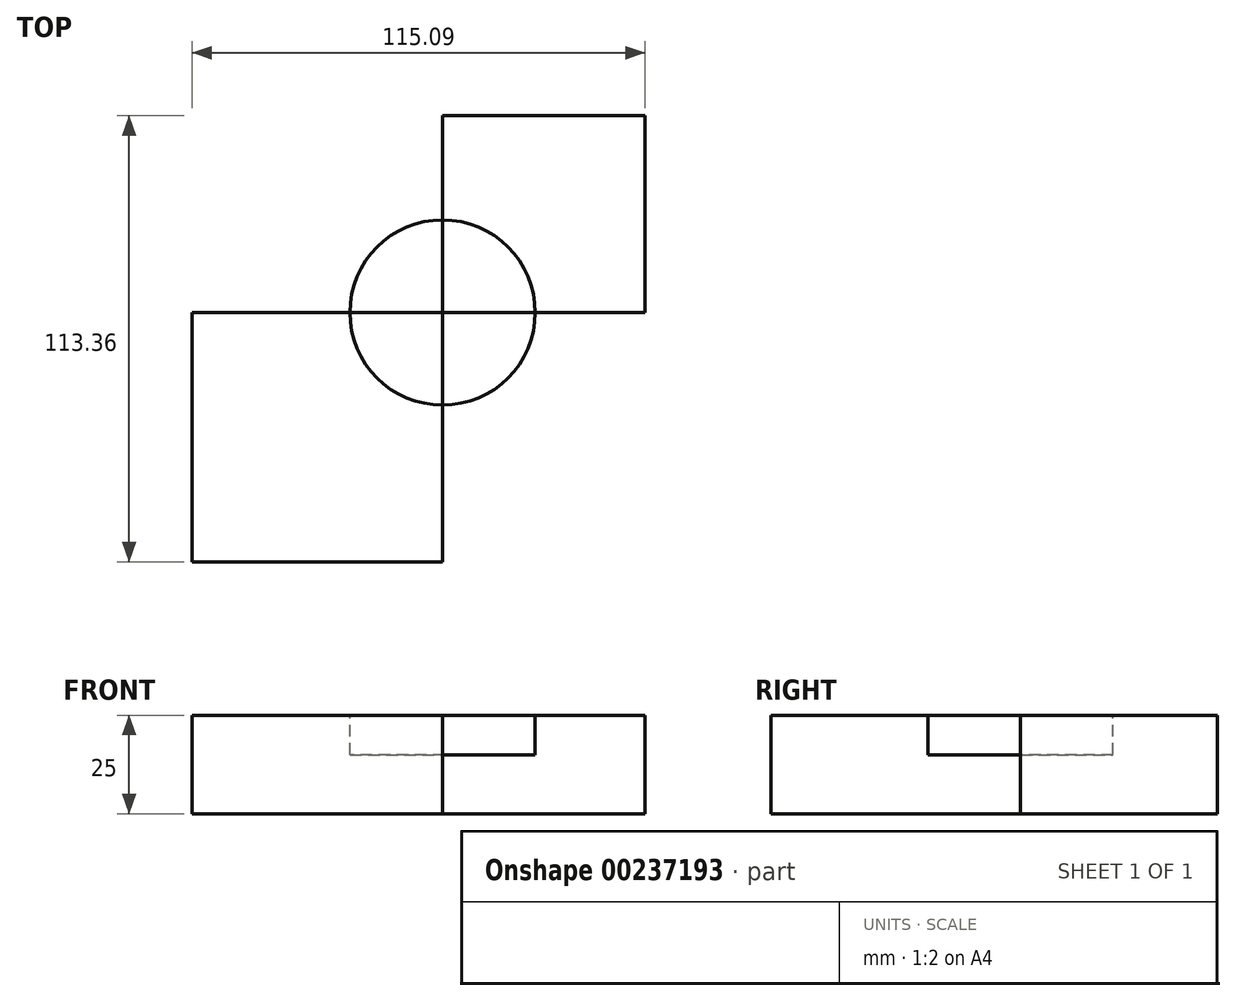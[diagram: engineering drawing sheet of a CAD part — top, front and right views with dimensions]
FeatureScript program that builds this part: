
annotation { "Feature Type Name" : "Feature", "Feature Type Description" : "" }
export const myFeature = defineFeature(function(context is Context, id is Id, definition is map)
    precondition{}
    {
        {
            var Q0;
            Q0=qCreatedBy(makeId("Top.planeOp"),FACE);
            var sketch = newSketch(context, id + "F0", { "sketchPlane" : qUnion([Q0])});
            skLineSegment(sketch, "E0.bottom", {"start": v(0, 0) * mm, "end": v(51.47, 0) * mm});
            skLineSegment(sketch, "E0.top", {"start": v(0, 50) * mm, "end": v(51.47, 50) * mm});
            skLineSegment(sketch, "E0.left", {"start": v(0, 0) * mm, "end": v(0, 50) * mm});
            skLineSegment(sketch, "E0.right", {"start": v(51.47, 0) * mm, "end": v(51.47, 50) * mm});
            skLineSegment(sketch, "E1.bottom", {"start": v(0, 0) * mm, "end": v(-63.62, 0) * mm});
            skLineSegment(sketch, "E1.top", {"start": v(0, -63.36) * mm, "end": v(-63.62, -63.36) * mm});
            skLineSegment(sketch, "E1.left", {"start": v(0, 0) * mm, "end": v(0, -63.36) * mm});
            skLineSegment(sketch, "E1.right", {"start": v(-63.62, 0) * mm, "end": v(-63.62, -63.36) * mm});
            skSolve(sketch);
        }
        {
            var Q0;
            Q0=makeQuery(id+"F0.imprint","IMPRINT",FACE,{"disambiguationData":[TD([[makeQuery(id+"F0.imprint","IMPRINT",EDGE,{"derivedFrom":sQuery(id+"F0.wireOp",EDGE,"E1.bottom")}),1.0]])]});
            var Q1;
            Q1=makeQuery(id+"F0.imprint","IMPRINT",FACE,{"disambiguationData":[TD([[makeQuery(id+"F0.imprint","IMPRINT",EDGE,{"derivedFrom":sQuery(id+"F0.wireOp",EDGE,"E0.bottom")}),1.0]])]});
            extrude(context, id + "F1", {"entities" : qUnion([Q0, Q1]), "depth" : 25 * mm});
        }
        {
            var Q0;
            Q0=makeQuery(id+"F1.opExtrude","CAP_FACE",FACE,{"disambiguationData":[OSD([sQuery(id+"F0.wireOp",EDGE,"E1.bottom"),sQuery(id+"F0.wireOp",EDGE,"E1.top"),sQuery(id+"F0.wireOp",EDGE,"E1.left"),sQuery(id+"F0.wireOp",EDGE,"E1.right")])],"isStart":false});
            var sketch = newSketch(context, id + "F2", { "sketchPlane" : qUnion([Q0])});
            skCircle(sketch, "E2", {"center": v(0, 0) * mm, "radius": 23.53 * mm});
            skSolve(sketch);
        }
        {
            var Q0;
            Q0 = qSketchRegion(id + "F2", true);
            extrude(context, id + "F3", {"entities" : qUnion([Q0]), "oppositeDirection" : true, "depth" : 10 * mm});
        }
    });
